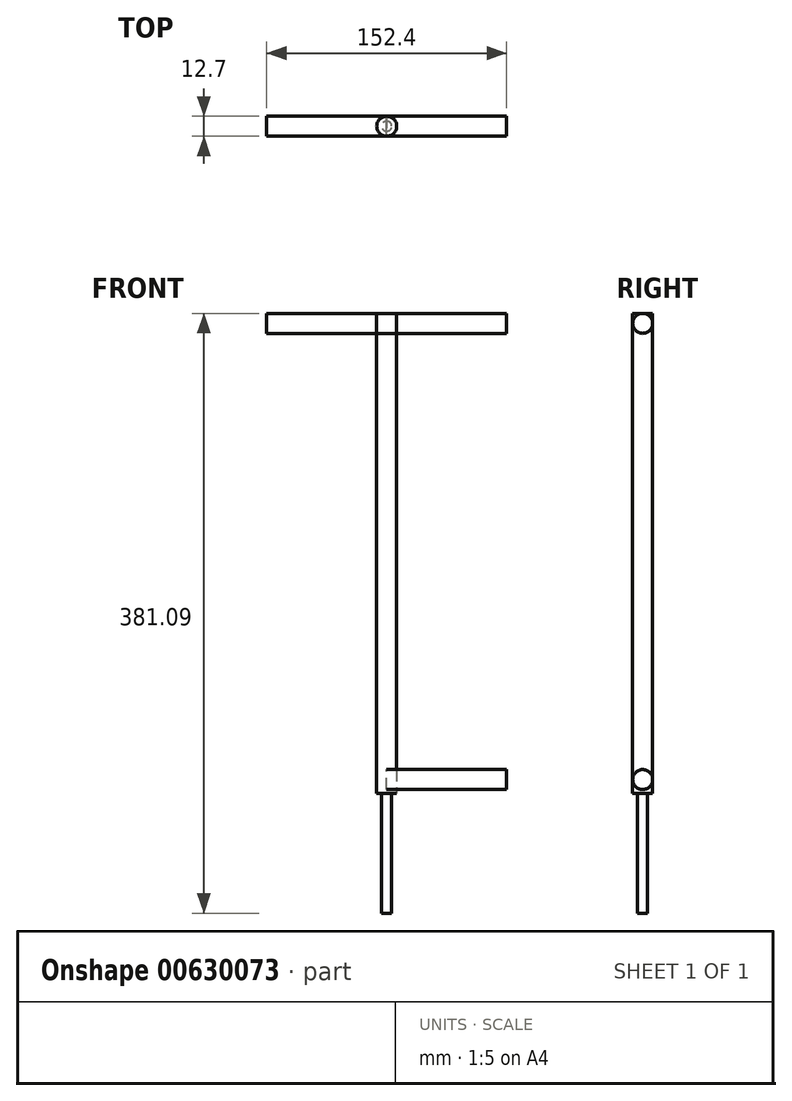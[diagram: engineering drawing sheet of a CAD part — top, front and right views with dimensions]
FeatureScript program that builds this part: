
annotation { "Feature Type Name" : "Feature", "Feature Type Description" : "" }
export const myFeature = defineFeature(function(context is Context, id is Id, definition is map)
    precondition{}
    {
        {
            var Q0;
            Q0=qCreatedBy(makeId("Top.planeOp"),FACE);
            var sketch = newSketch(context, id + "F0", { "sketchPlane" : qUnion([Q0])});
            skCircle(sketch, "E0", {"center": v(0, 0) * mm, "radius": 6.35 * mm});
            skSolve(sketch);
        }
        {
            var Q0;
            Q0 = qSketchRegion(id + "F0", true);
            extrude(context, id + "F1", {"entities" : qUnion([Q0]), "endBound" : BoundingType.SYMMETRIC, "depth" : 304.8 * mm, "offsetDistance" : 25.4 * mm});
        }
        {
            var Q0;
            Q0=qCreatedBy(makeId("Right.planeOp"),FACE);
            var sketch = newSketch(context, id + "F2", { "sketchPlane" : qUnion([Q0])});
            skCircle(sketch, "E1", {"center": v(0, 146.14) * mm, "radius": 6.35 * mm});
            skSolve(sketch);
        }
        {
            var Q0;
            Q0 = qSketchRegion(id + "F2", true);
            extrude(context, id + "F3", {"entities" : qUnion([Q0]), "endBound" : BoundingType.SYMMETRIC, "depth" : 152.4 * mm, "offsetDistance" : 25.4 * mm});
        }
        {
            var Q0;
            Q0=qCreatedBy(makeId("Right.planeOp"),FACE);
            var sketch = newSketch(context, id + "F4", { "sketchPlane" : qUnion([Q0])});
            skCircle(sketch, "E2", {"center": v(0, -143.65) * mm, "radius": 6.35 * mm});
            skSolve(sketch);
        }
        {
            var Q0;
            Q0 = qSketchRegion(id + "F4", true);
            extrude(context, id + "F5", {"entities" : qUnion([Q0]), "depth" : 76.2 * mm, "offsetDistance" : 25.4 * mm});
        }
        {
            var Q0;
            Q0=makeQuery(id+"F1.opExtrude","CAP_FACE",FACE,{"disambiguationData":[OSD([sQuery(id+"F0.wireOp",EDGE,"E0")])],"isStart":true});
            var sketch = newSketch(context, id + "F6", { "sketchPlane" : qUnion([Q0])});
            skCircle(sketch, "E3", {"center": v(0, 0) * mm, "radius": 3.17 * mm});
            skSolve(sketch);
        }
        {
            var Q0;
            Q0 = qSketchRegion(id + "F6", true);
            extrude(context, id + "F7", {"entities" : qUnion([Q0]), "operationType" : NewBodyOperationType.ADD, "depth" : 76.2 * mm, "offsetDistance" : 25.4 * mm});
        }
    });
